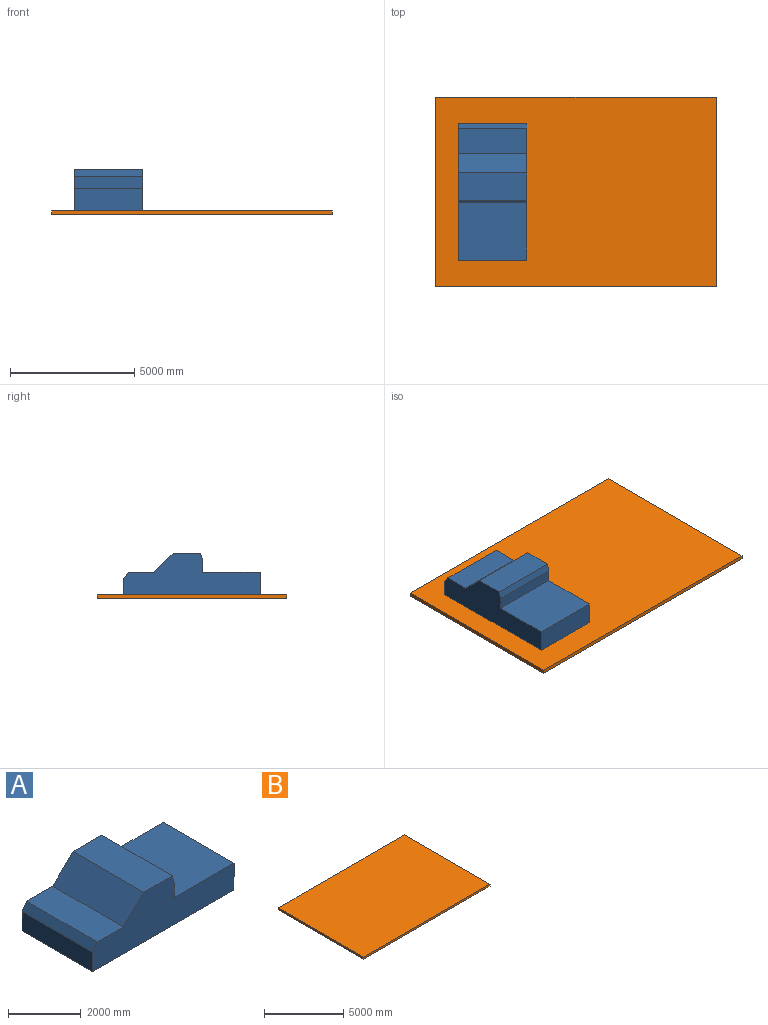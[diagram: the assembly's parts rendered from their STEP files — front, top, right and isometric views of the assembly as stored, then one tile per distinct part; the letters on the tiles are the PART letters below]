
ASSEMBLY  parts=2 mates=1
PART A: 12 faces, bbox 5486.4x2743.2x1676.4 mm
  f0: plane 2743.2x1111.77mm, normal (0,0,1), area 3049806.9mm2, adj f1,f2,f7,f11
  f1: plane 5486.4x1676.4mm, normal (0,-1,0), area 6158699mm2, adj f0,f3,f4,f5,f6,f7,f8,f9
  f2: plane 5486.4x1676.4mm, normal (0,1,0), area 6158699mm2, adj f0,f3,f4,f5,f6,f7,f8,f9
  f3: plane 5486.4x2743.2mm, normal (0,0,-1), area 15050292.5mm2, adj f1,f2,f4,f5
  f4: plane 2743.2x906.79mm, normal (1,0,0), area 2487509.6mm2, adj f1,f2,f3,f8
  f5: plane 2743.2x648.4mm, normal (-1,0,0), area 1778690.2mm2, adj f1,f2,f3,f9
  f6: plane 2743.2x469.03mm, normal (1,0,0), area 1286651.1mm2, adj f1,f2,f7,f8
  f7: plane 2743.2x300.58mm, normal (0.97,0,0.25), area 851742.4mm2, adj f0,f1,f2,f6
  f8: plane 2743.2x2316.25mm, normal (0,0,1), area 6353927.5mm2, adj f1,f2,f4,f6
  f9: plane 2743.2x258.39mm, normal (-0.82,0,0.57), area 864500.5mm2, adj f1,f2,f5,f10
  f10: plane 2743.2x1012.32mm, normal (0,0,1), area 2777002.4mm2, adj f1,f2,f9,f11
  f11: plane 2743.2x787.8mm, normal (-0.7,0,0.72), area 3021176.1mm2, adj f0,f1,f2,f10
PART B: 6 faces, bbox 11277.6x7620x152.4 mm
  f0: plane 11277.6x7620mm, normal (0,0,-1), area 85935312mm2, adj f1,f3,f4,f5
  f1: plane 7620x152.4mm, normal (-1,0,0), area 1161288mm2, adj f0,f2,f3,f4
  f2: plane 11277.6x7620mm, normal (0,0,1), area 85935312mm2, adj f1,f3,f4,f5
  f3: plane 11277.6x152.4mm, normal (0,1,0), area 1718706.2mm2, adj f0,f1,f2,f5
  f4: plane 11277.6x152.4mm, normal (0,-1,0), area 1718706.2mm2, adj f0,f1,f2,f5
  f5: plane 7620x152.4mm, normal (1,0,0), area 1161288mm2, adj f0,f2,f3,f4
PLACE A rot(axis=(0,0,-1),90deg) t=(949.85,4446.34,2237.18)mm
PLACE B t=(187.85,-1954.46,2237.18)mm fixed
MATE fastened B.f2 <-> A.f3  axis (0,0,1) through (35.45,1703.14,2237.18)mm
